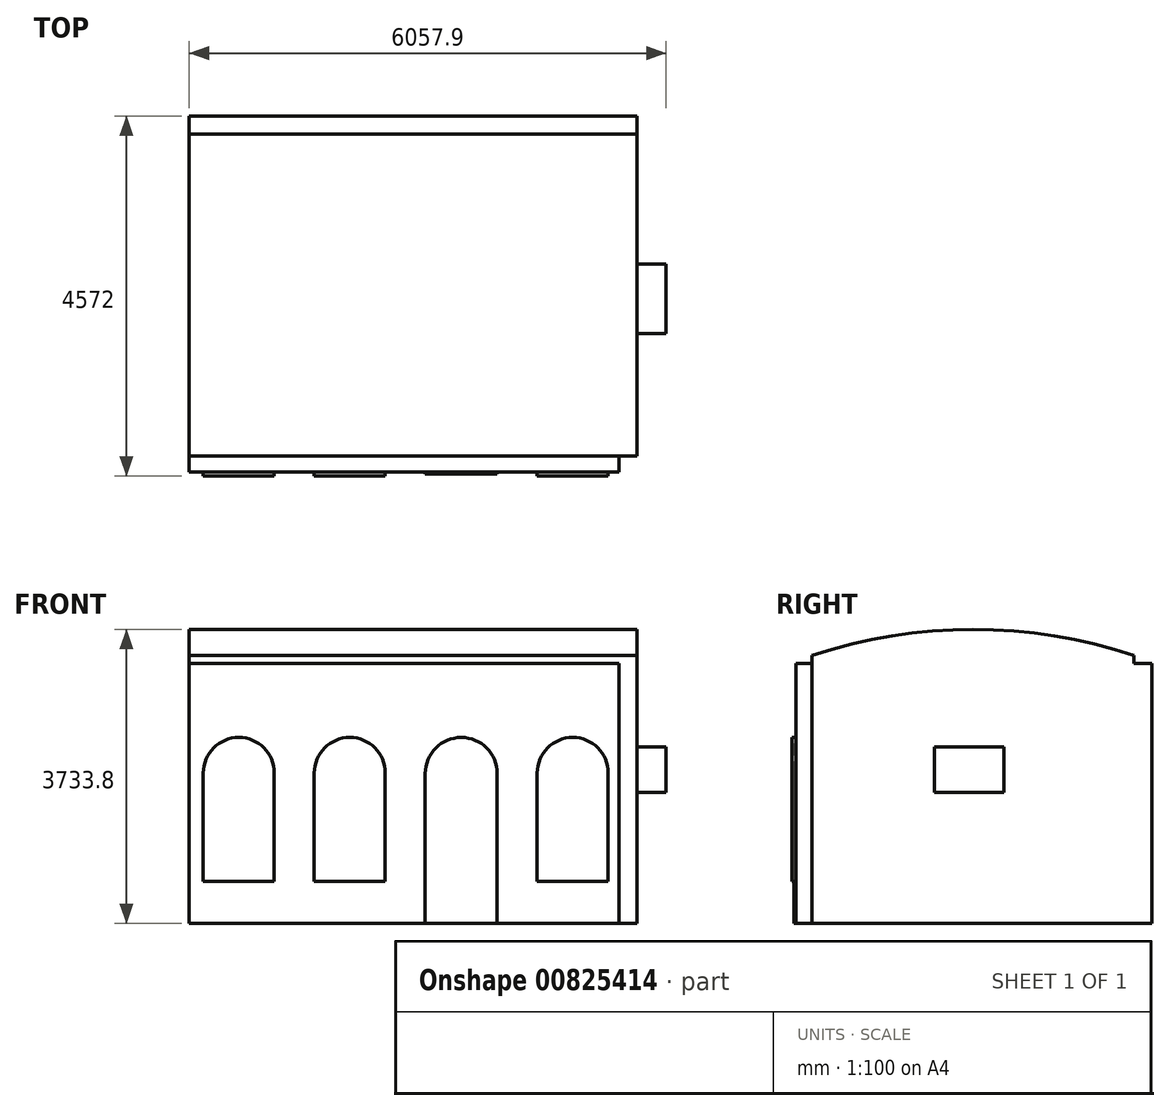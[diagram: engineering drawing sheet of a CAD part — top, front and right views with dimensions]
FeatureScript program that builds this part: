
annotation { "Feature Type Name" : "Feature", "Feature Type Description" : "" }
export const myFeature = defineFeature(function(context is Context, id is Id, definition is map)
    precondition{}
    {
        {
            var Q0;
            Q0=qCreatedBy(makeId("Top.planeOp"),FACE);
            var sketch = newSketch(context, id + "F0", { "sketchPlane" : qUnion([Q0])});
            skLineSegment(sketch, "E0.bottom", {"start": v(-2709.93, 2244.88) * mm, "end": v(2979.67, 2244.88) * mm});
            skLineSegment(sketch, "E0.top", {"start": v(-2709.93, -2276.32) * mm, "end": v(2979.67, -2276.32) * mm});
            skLineSegment(sketch, "E0.left", {"start": v(-2709.93, 2244.88) * mm, "end": v(-2709.93, -2276.32) * mm});
            skLineSegment(sketch, "E0.right", {"start": v(2979.67, 2244.88) * mm, "end": v(2979.67, -2276.32) * mm});
            skSolve(sketch);
        }
        {
            var Q0;
            Q0 = qSketchRegion(id + "F0", true);
            var Q1;
            Q1=makeQuery(id+"F0.imprint","IMPRINT",FACE,{"disambiguationData":[TD([[makeQuery(id+"F0.imprint","IMPRINT",EDGE,{"derivedFrom":sQuery(id+"F0.wireOp",EDGE,"E0.bottom")}),-1.0]])]});
            extrude(context, id + "F1", {"entities" : qUnion([Q0, Q1]), "depth" : 3302 * mm, "offsetDistance" : 25.4 * mm});
        }
        {
            var Q0;
            Q0=makeQuery(id+"F1.opExtrude","CAP_FACE",FACE,{"disambiguationData":[OSD([sQuery(id+"F0.wireOp",EDGE,"E0.bottom"),sQuery(id+"F0.wireOp",EDGE,"E0.top"),sQuery(id+"F0.wireOp",EDGE,"E0.left"),sQuery(id+"F0.wireOp",EDGE,"E0.right")])],"isStart":false});
            var sketch = newSketch(context, id + "F2", { "sketchPlane" : qUnion([Q0])});
            skLineSegment(sketch, "E1", {"start": v(-2709.93, 2016.28) * mm, "end": v(2979.67, 2016.28) * mm});
            skLineSegment(sketch, "E2", {"start": v(-2709.93, -2073.12) * mm, "end": v(2979.67, -2073.12) * mm});
            skSolve(sketch);
        }
        {
            var Q0;
            {var subQ0=sQuery(id+"F2.wireOp",EDGE,"E1");Q0=makeQuery(id+"F2.imprint","IMPRINT",FACE,{"disambiguationData":[TD([[makeQuery(id+"F2.imprint","IMPRINT",EDGE,{"derivedFrom":subQ0}),-1.0]])]});}
            extrude(context, id + "F3", {"entities" : qUnion([Q0]), "operationType" : NewBodyOperationType.ADD, "depth" : 101.6 * mm, "offsetDistance" : 25.4 * mm});
        }
        {
            var Q0;
            {var subQ0=sQuery(id+"F0.wireOp",EDGE,"E0.right");Q0=makeQuery(id+"F3.boolean.opBoolean","MERGE",FACE,{"derivedFrom":[makeQuery(id+"F1.opExtrude","SWEPT_FACE",FACE,{"disambiguationData":[OSD([subQ0])]}),makeQuery(id+"F3.opExtrude","SWEPT_FACE",FACE,{"disambiguationData":[OSD([subQ0])]})]});}
            var sketch = newSketch(context, id + "F4", { "sketchPlane" : qUnion([Q0])});
            skArc(sketch, "E3", {"start": v(2016.28, 3403.6) * mm, "mid": v(-28.42, 3733.8) * mm, "end": v(-2073.12, 3403.6) * mm});
            skPoint(sketch, "E4", {"position": v(-28.42, 3403.6) * mm});
            skLineSegment(sketch, "E5", {"start": v(-28.42, 3403.6) * mm, "end": v(-28.42, 3733.8) * mm, "construction": true});
            skLineSegment(sketch, "E6", {"start": v(-28.42, 3733.8) * mm, "end": v(-28.42, 0) * mm});
            skSolve(sketch);
        }
        {
            var Q0;
            {var subQ0=sQuery(id+"F4.wireOp",EDGE,"E3");var subQ4=sQuery(id+"F4.wireOp",EDGE,"E6");var subQ5=makeQuery(id+"F4.imprint","INTERSECT",VERTEX,{"derivedFrom":[subQ0,subQ4]});Q0=makeQuery(id+"F4.imprint","IMPRINT",FACE,{"disambiguationData":[TD([[makeQuery(id+"F4.imprint","IMPRINT",EDGE,{"disambiguationData":[TD([[subQ5,-1.0]])],"derivedFrom":subQ4}),1.0]])]});}
            var Q1;
            {var subQ0=sQuery(id+"F4.wireOp",EDGE,"E3");var subQ4=sQuery(id+"F4.wireOp",EDGE,"E6");var subQ5=makeQuery(id+"F4.imprint","INTERSECT",VERTEX,{"derivedFrom":[subQ0,subQ4]});Q1=makeQuery(id+"F4.imprint","IMPRINT",FACE,{"disambiguationData":[TD([[makeQuery(id+"F4.imprint","IMPRINT",EDGE,{"disambiguationData":[TD([[subQ5,-1.0]])],"derivedFrom":subQ4}),-1.0]])]});}
            var Q2;
            {var subQ0=sQuery(id+"F0.wireOp",EDGE,"E0.left");Q2=makeQuery(id+"F3.boolean.opBoolean","MERGE",FACE,{"derivedFrom":[makeQuery(id+"F1.opExtrude","SWEPT_FACE",FACE,{"disambiguationData":[OSD([subQ0])]}),makeQuery(id+"F3.opExtrude","SWEPT_FACE",FACE,{"disambiguationData":[OSD([subQ0])]})]});}
            extrude(context, id + "F5", {"entities" : qUnion([Q0, Q1]), "operationType" : NewBodyOperationType.ADD, "endBound" : BoundingType.UP_TO_SURFACE, "oppositeDirection" : true, "depth" : 25.4 * mm, "endBoundEntityFace" : qUnion([Q2]), "offsetDistance" : 25.4 * mm});
        }
        {
            var Q0;
            {var subQ0=sQuery(id+"F0.wireOp",EDGE,"E0.right");Q0=makeQuery(id+"F5.boolean.opBoolean","MERGE",FACE,{"derivedFrom":[makeQuery(id+"F3.boolean.opBoolean","MERGE",FACE,{"derivedFrom":[makeQuery(id+"F1.opExtrude","SWEPT_FACE",FACE,{"disambiguationData":[OSD([subQ0])]}),makeQuery(id+"F3.opExtrude","SWEPT_FACE",FACE,{"disambiguationData":[OSD([subQ0])]})]}),makeQuery(id+"F5.opExtrude","CAP_FACE",FACE,{"disambiguationData":[OSD([subQ0,sQuery(id+"F4.wireOp",EDGE,"E3")])],"isStart":true})]});}
            var sketch = newSketch(context, id + "F6", { "sketchPlane" : qUnion([Q0])});
            skLineSegment(sketch, "E7.bottom", {"start": v(-517.37, 2241.55) * mm, "end": v(365.28, 2241.55) * mm});
            skLineSegment(sketch, "E7.top", {"start": v(-517.37, 1663.7) * mm, "end": v(365.28, 1663.7) * mm});
            skLineSegment(sketch, "E7.left", {"start": v(-517.37, 2241.55) * mm, "end": v(-517.37, 1663.7) * mm});
            skLineSegment(sketch, "E7.right", {"start": v(365.28, 2241.55) * mm, "end": v(365.28, 1663.7) * mm});
            skSolve(sketch);
        }
        {
            var Q0;
            Q0=makeQuery(id+"F6.imprint","IMPRINT",FACE,{"disambiguationData":[TD([[makeQuery(id+"F6.imprint","IMPRINT",EDGE,{"derivedFrom":sQuery(id+"F6.wireOp",EDGE,"E7.bottom")}),-1.0]])]});
            extrude(context, id + "F7", {"entities" : qUnion([Q0]), "operationType" : NewBodyOperationType.ADD, "depth" : 368.3 * mm, "offsetDistance" : 25.4 * mm});
        }
        {
            var Q0;
            Q0=makeQuery(id+"F1.opExtrude","SWEPT_FACE",FACE,{"disambiguationData":[OSD([sQuery(id+"F0.wireOp",EDGE,"E0.top")])]});
            var sketch = newSketch(context, id + "F8", { "sketchPlane" : qUnion([Q0])});
            skLineSegment(sketch, "E8", {"start": v(-2709.93, 508) * mm, "end": v(2979.67, 508) * mm, "construction": true});
            skLineSegment(sketch, "E9.bottom", {"start": v(-2532.13, 533.4) * mm, "end": v(-1630.43, 533.4) * mm});
            skLineSegment(sketch, "E9.top", {"start": v(-2532.13, 1911.35) * mm, "end": v(-1630.43, 1911.35) * mm});
            skLineSegment(sketch, "E9.left", {"start": v(-2532.13, 533.4) * mm, "end": v(-2532.13, 1911.35) * mm});
            skLineSegment(sketch, "E9.right", {"start": v(-1630.43, 533.4) * mm, "end": v(-1630.43, 1911.35) * mm});
            skLineSegment(sketch, "E10.bottom", {"start": v(-1122.43, 533.4) * mm, "end": v(-220.73, 533.4) * mm});
            skLineSegment(sketch, "E10.top", {"start": v(-1122.43, 1911.35) * mm, "end": v(-220.73, 1911.35) * mm});
            skLineSegment(sketch, "E10.left", {"start": v(-1122.43, 533.4) * mm, "end": v(-1122.43, 1911.35) * mm});
            skLineSegment(sketch, "E10.right", {"start": v(-220.73, 533.4) * mm, "end": v(-220.73, 1911.35) * mm});
            skLineSegment(sketch, "E11.bottom", {"start": v(287.27, 0) * mm, "end": v(1201.67, 0) * mm});
            skLineSegment(sketch, "E11.top", {"start": v(287.27, 1905) * mm, "end": v(1201.67, 1905) * mm});
            skLineSegment(sketch, "E11.left", {"start": v(287.27, 0) * mm, "end": v(287.27, 1905) * mm});
            skLineSegment(sketch, "E11.right", {"start": v(1201.67, 0) * mm, "end": v(1201.67, 1905) * mm});
            skLineSegment(sketch, "E12.bottom", {"start": v(1709.67, 533.4) * mm, "end": v(2611.37, 533.4) * mm});
            skLineSegment(sketch, "E12.top", {"start": v(1709.67, 1911.35) * mm, "end": v(2611.37, 1911.35) * mm});
            skLineSegment(sketch, "E12.left", {"start": v(1709.67, 533.4) * mm, "end": v(1709.67, 1911.35) * mm});
            skLineSegment(sketch, "E12.right", {"start": v(2611.37, 533.4) * mm, "end": v(2611.37, 1911.35) * mm});
            skPoint(sketch, "E13", {"position": v(796.39, 0) * mm});
            skArc(sketch, "E14", {"start": v(-1630.43, 1911.35) * mm, "mid": v(-2081.28, 2362.2) * mm, "end": v(-2532.13, 1911.35) * mm});
            skArc(sketch, "E15", {"start": v(-220.73, 1911.35) * mm, "mid": v(-671.58, 2362.2) * mm, "end": v(-1122.43, 1911.35) * mm});
            skArc(sketch, "E16", {"start": v(1201.67, 1905) * mm, "mid": v(744.47, 2362.2) * mm, "end": v(287.27, 1905) * mm});
            skArc(sketch, "E17", {"start": v(2611.37, 1911.35) * mm, "mid": v(2160.52, 2362.2) * mm, "end": v(1709.67, 1911.35) * mm});
            skPoint(sketch, "E18", {"position": v(-2081.28, 2362.2) * mm});
            skPoint(sketch, "E19", {"position": v(-671.58, 2362.2) * mm});
            skPoint(sketch, "E20", {"position": v(744.47, 2362.2) * mm});
            skPoint(sketch, "E21", {"position": v(2160.52, 2362.2) * mm});
            skLineSegment(sketch, "E22", {"start": v(2751.07, 3302) * mm, "end": v(2751.07, 0) * mm});
            skSolve(sketch);
        }
        {
            var Q0;
            {var subQ0=sQuery(id+"F8.wireOp",EDGE,"E22");Q0=makeQuery(id+"F8.imprint","IMPRINT",FACE,{"disambiguationData":[TD([[makeQuery(id+"F8.imprint","IMPRINT",EDGE,{"derivedFrom":subQ0}),1.0]])]});}
            var Q1;
            Q1=makeQuery(id+"F3.opExtrude","SWEPT_FACE",FACE,{"disambiguationData":[OSD([sQuery(id+"F2.wireOp",EDGE,"E2")])]});
            extrude(context, id + "F9", {"entities" : qUnion([Q0]), "operationType" : NewBodyOperationType.REMOVE, "endBound" : BoundingType.UP_TO_SURFACE, "oppositeDirection" : true, "depth" : 25.4 * mm, "endBoundEntityFace" : qUnion([Q1]), "offsetDistance" : 25.4 * mm});
        }
        {
            var Q0;
            Q0=makeQuery(id+"F8.imprint","IMPRINT",FACE,{"disambiguationData":[TD([[makeQuery(id+"F8.imprint","IMPRINT",EDGE,{"derivedFrom":sQuery(id+"F8.wireOp",EDGE,"E9.bottom")}),1.0]])]});
            var Q1;
            Q1=makeQuery(id+"F8.imprint","IMPRINT",FACE,{"disambiguationData":[TD([[makeQuery(id+"F8.imprint","IMPRINT",EDGE,{"derivedFrom":sQuery(id+"F8.wireOp",EDGE,"E9.top")}),1.0]])]});
            var Q2;
            Q2=makeQuery(id+"F8.imprint","IMPRINT",FACE,{"disambiguationData":[TD([[makeQuery(id+"F8.imprint","IMPRINT",EDGE,{"derivedFrom":sQuery(id+"F8.wireOp",EDGE,"E10.bottom")}),1.0]])]});
            var Q3;
            Q3=makeQuery(id+"F8.imprint","IMPRINT",FACE,{"disambiguationData":[TD([[makeQuery(id+"F8.imprint","IMPRINT",EDGE,{"derivedFrom":sQuery(id+"F8.wireOp",EDGE,"E10.top")}),1.0]])]});
            var Q4;
            Q4=makeQuery(id+"F8.imprint","IMPRINT",FACE,{"disambiguationData":[TD([[makeQuery(id+"F8.imprint","IMPRINT",EDGE,{"derivedFrom":sQuery(id+"F8.wireOp",EDGE,"E12.bottom")}),1.0]])]});
            var Q5;
            Q5=makeQuery(id+"F8.imprint","IMPRINT",FACE,{"disambiguationData":[TD([[makeQuery(id+"F8.imprint","IMPRINT",EDGE,{"derivedFrom":sQuery(id+"F8.wireOp",EDGE,"E12.top")}),1.0]])]});
            extrude(context, id + "F10", {"entities" : qUnion([Q0, Q1, Q2, Q3, Q4, Q5]), "operationType" : NewBodyOperationType.ADD, "depth" : 50.8 * mm, "offsetDistance" : 25.4 * mm});
        }
        {
            var Q0;
            Q0=makeQuery(id+"F8.imprint","IMPRINT",FACE,{"disambiguationData":[TD([[makeQuery(id+"F8.imprint","IMPRINT",EDGE,{"derivedFrom":sQuery(id+"F8.wireOp",EDGE,"E11.bottom")}),1.0]])]});
            var Q1;
            Q1=makeQuery(id+"F8.imprint","IMPRINT",FACE,{"disambiguationData":[TD([[makeQuery(id+"F8.imprint","IMPRINT",EDGE,{"derivedFrom":sQuery(id+"F8.wireOp",EDGE,"E11.top")}),1.0]])]});
            extrude(context, id + "F11", {"entities" : qUnion([Q0, Q1]), "operationType" : NewBodyOperationType.ADD, "depth" : 25.4 * mm, "offsetDistance" : 25.4 * mm});
        }
    });
